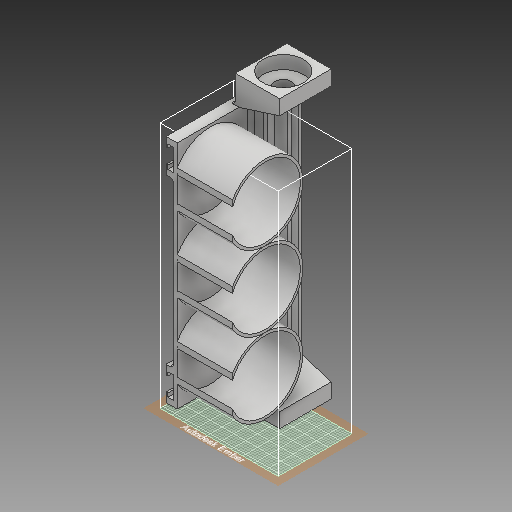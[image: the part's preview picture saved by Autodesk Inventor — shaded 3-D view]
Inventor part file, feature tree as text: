
AUTODESK INVENTOR PART (.ipt)
format: ipt  version: 2018 (Build 220112000, 112)  size: 797,696 bytes
history: native  units: mm
features: sketch x39, extrude x28, fillet x4, chamfer x2
ambient origin geometry x8: Origin, YZ Plane, XZ Plane, XY Plane, X Axis, Y Axis, Z Axis, Center Point
bodies: Solid1 (feature_tree)
feature tree (73):
  extrude  "Extrusion1"  Depth=125.0mm
  extrude  "Extrusion2"  Depth=2.0mm
  extrude  "Extrusion3"  Depth=2.0mm TaperAngle=0.0deg
  extrude  "Extrusion4"  Depth=7.1mm TaperAngle=0.0deg
  extrude  "Extrusion5"  Depth=155.0mm TaperAngle=0.0deg
  chamfer  "Chamfer1"  Distance=7.1mm
  sketch  "Sketch6"  dims[d16=22.0mm d17=7.1mm d18=0.0mm d19=7.0mm d20=2.0mm d21=12.61873mm]
  chamfer  "Chamfer2"  Distance=2.0mm
  sketch  "Sketch7"  dims[d22=7.0mm d23=2.0mm d24=12.61873mm d25=8.0mm]
  sketch  "Sketch8"  dims[d26=2.0mm d27=0.0mm d28=8.0mm]
  sketch  "Sketch9"  dims[d29=2.0mm d30=0.0mm d31=2.0mm d32=0.0mm]
  extrude  "Extrusion6"  Depth=2.0mm
  extrude  "Extrusion7"  Depth=2.0mm
  extrude  "Extrusion8"  Depth=2.0mm TaperAngle=0.0deg
  extrude  "Extrusion9"  Depth=2.0mm
  sketch  "Sketch13"  dims[d45=2.0mm d46=38.0mm]
  sketch  "Sketch14"  dims[d47=2.0mm d48=0.0mm d49=38.0mm]
  extrude  "Extrusion10"  Depth=2.0mm
  sketch  "Sketch16"  dims[d53=38.0mm d54=40.75mm]
  extrude  "Extrusion11"  Depth=2.0mm TaperAngle=0.0deg
  fillet  "Fillet1"  Radius=2.0mm
  fillet  "Fillet2"  Radius=2.0mm
  extrude  "Extrusion12"  Depth=2.0mm
  extrude  "Extrusion13"  Depth=2.0mm
  extrude  "Extrusion14"  Depth=21.75mm
  sketch  "Sketch21"  dims[d67=12.0mm d68=3.0mm]
  extrude  "Extrusion15"  Depth=40.75mm
  extrude  "Extrusion16"  Depth=40.75mm
  sketch  "Sketch24"  dims[d75=5.0mm d76=5.0mm]
  sketch  "Sketch25"  dims[d77=5.0mm d78=5.0mm]
  extrude  "Extrusion17"  Depth=32.0mm TaperAngle=0.0deg
  extrude  "Extrusion18"  Depth=12.0mm
  sketch  "Sketch28"  dims[d85=30.0mm d86=0.0mm d87=30.0mm d88=0.0mm]
  fillet  "Fillet3"  Radius=3.0mm
  extrude  "Extrusion19"  Depth=3.0mm
  extrude  "Extrusion20"  Depth=3.0mm
  sketch  "Sketch31"  dims[d96=10.0mm]
  extrude  "Extrusion21"  Depth=2.0mm
  extrude  "Extrusion22"  Depth=2.0mm TaperAngle=0.0deg
  extrude  "Extrusion23"  Depth=5.0mm
  extrude  "Extrusion24"  Depth=5.0mm
  extrude  "Extrusion25"  Depth=9.375mm
  extrude  "Extrusion26"  Depth=2.0mm TaperAngle=0.0deg
  extrude  "Extrusion27"  Depth=30.0mm TaperAngle=0.0deg
  extrude  "Extrusion28"  Depth=28.0mm TaperAngle=0.0deg
  fillet  "Fillet4"  Radius=4.0mm
  sketch  "Sketch1"  dims[d0=24.0mm d1=125.0mm]
  sketch  "Sketch2"  dims[d2=2.0mm d3=0.0mm d4=15.0mm]
  sketch  "Sketch3"  dims[d5=15.0mm d6=22.0mm d7=2.0mm d8=0.0mm d9=0.0mm]
  sketch  "Sketch4"  dims[d10=22.0mm d11=7.1mm d12=0.0mm]
  sketch  "Sketch5"  dims[d13=9.0mm d14=155.0mm d15=0.0mm]
  sketch  "Sketch10"  dims[d33=2.0mm d34=0.0mm d35=5.5mm]
  sketch  "Sketch11"  dims[d36=11.0mm d37=2.0mm]
  sketch  "Sketch12"  dims[d38=2.0mm d39=7.0mm d40=0.0mm d42=2.0mm d43=0.0mm d44=2.0mm]
  sketch  "Sketch15"  dims[d51=43.5mm d52=21.75mm]
  sketch  "Sketch17"  dims[d55=38.0mm d56=40.75mm]
  sketch  "Sketch18"  dims[d57=30.0mm d58=0.0mm d59=32.0mm d60=0.0mm]
  sketch  "Sketch19"  dims[d61=3.0mm d62=12.0mm d63=3.0mm]
  sketch  "Sketch20"  dims[d64=3.1mm d65=0.0mm d66=3.0mm]
  sketch  "Sketch22"  dims[d69=3.1mm d70=0.0mm d71=2.0mm]
  sketch  "Sketch23"  dims[d72=2.0mm d73=3.6mm d74=0.0mm]
  sketch  "Sketch26"  dims[d79=1.0mm d80=0.0mm d81=9.375mm]
  sketch  "Sketch27"  dims[d82=2.0mm d83=100.0mm d84=0.0mm]
  sketch  "Sketch29"  dims[d89=8.0mm d90=0.0mm d91=28.0mm d92=0.0mm d93=4.0mm]
  sketch  "Sketch30"  dims[d94=169.0mm d95=0.0mm]
  sketch  "Sketch32"  dims[d97=4.0mm d98=0.0mm]
  sketch  "Sketch33"  dims[d99=4.0mm d100=0.0mm]
  sketch  "Sketch34"  dims[d101=6.35mm]
  sketch  "Sketch35"  dims[d102=40.0mm d103=0.0mm]
  sketch  "Sketch36"  dims[d104=1.0mm]
  sketch  "Sketch37"  dims[d105=1.0mm]
  sketch  "Sketch38"  dims[d106=5.0mm d107=0.0mm]
  sketch  "Sketch39"  dims[d108=2.0mm]
